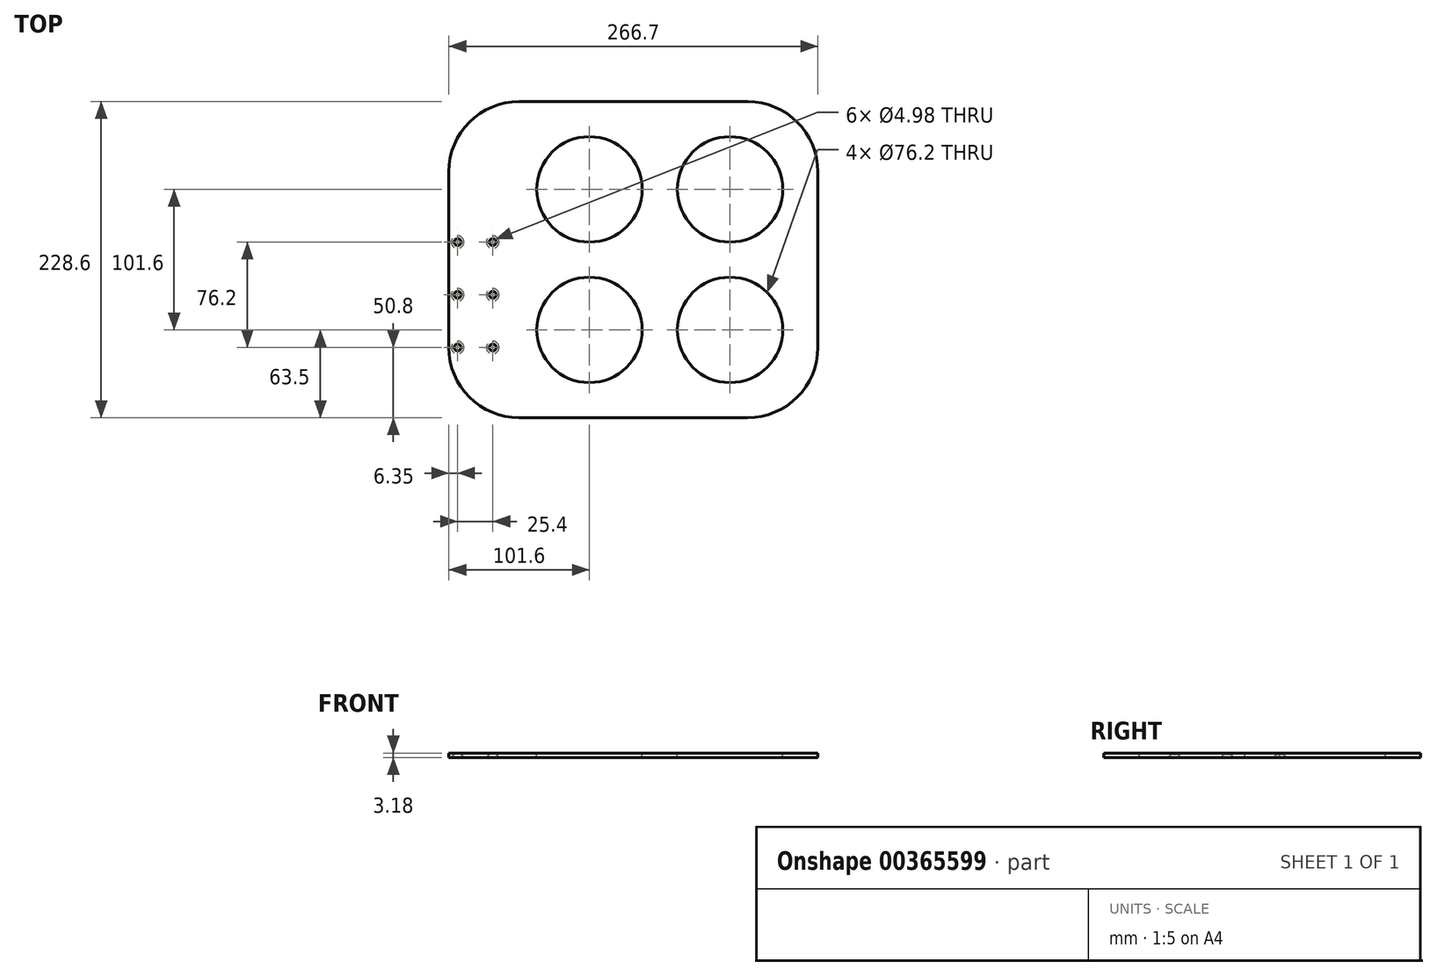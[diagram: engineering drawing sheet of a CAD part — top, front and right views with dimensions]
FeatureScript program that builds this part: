
annotation { "Feature Type Name" : "Feature", "Feature Type Description" : "" }
export const myFeature = defineFeature(function(context is Context, id is Id, definition is map)
    precondition{}
    {
        {
            var Q0;
            Q0=qCreatedBy(makeId("Top.planeOp"),FACE);
            var sketch = newSketch(context, id + "F0", { "sketchPlane" : qUnion([Q0])});
            skLineSegment(sketch, "E0.bottom", {"start": v(133.35, -114.3) * mm, "end": v(-133.35, -114.3) * mm});
            skLineSegment(sketch, "E0.top", {"start": v(133.35, 114.3) * mm, "end": v(-133.35, 114.3) * mm});
            skLineSegment(sketch, "E0.left", {"start": v(133.35, -114.3) * mm, "end": v(133.35, 114.3) * mm});
            skLineSegment(sketch, "E0.right", {"start": v(-133.35, -114.3) * mm, "end": v(-133.35, 114.3) * mm});
            skPoint(sketch, "E0.middle", {"position": v(0, 0) * mm});
            skSolve(sketch);
        }
        {
            var Q0;
            Q0=makeQuery(id+"F0.imprint","IMPRINT",FACE,{"disambiguationData":[TD([[makeQuery(id+"F0.imprint","IMPRINT",EDGE,{"derivedFrom":sQuery(id+"F0.wireOp",EDGE,"E0.bottom")}),-1.0]])]});
            extrude(context, id + "F1", {"entities" : qUnion([Q0]), "depth" : 3.17 * mm, "offsetDistance" : 25.4 * mm});
        }
        {
            var Q0;
            Q0=makeQuery(id+"F1.opExtrude","SWEPT_EDGE",EDGE,{"disambiguationData":[OSD([sQuery(id+"F0.wireOp",EDGE,"E0.top"),sQuery(id+"F0.wireOp",EDGE,"E0.right")])]});
            var Q1;
            Q1=makeQuery(id+"F1.opExtrude","SWEPT_EDGE",EDGE,{"disambiguationData":[OSD([sQuery(id+"F0.wireOp",EDGE,"E0.top"),sQuery(id+"F0.wireOp",EDGE,"E0.left")])]});
            var Q2;
            Q2=makeQuery(id+"F1.opExtrude","SWEPT_EDGE",EDGE,{"disambiguationData":[OSD([sQuery(id+"F0.wireOp",EDGE,"E0.bottom"),sQuery(id+"F0.wireOp",EDGE,"E0.left")])]});
            var Q3;
            Q3=makeQuery(id+"F1.opExtrude","SWEPT_EDGE",EDGE,{"disambiguationData":[OSD([sQuery(id+"F0.wireOp",EDGE,"E0.bottom"),sQuery(id+"F0.wireOp",EDGE,"E0.right")])]});
            fillet(context, id + "F2", {"entities" : qUnion([Q0, Q1, Q2, Q3]), "radius" : 50.8 * mm, "tangentPropagation" : true, "allowEdgeOverflow" : false});
        }
        {
            var Q0;
            Q0=makeQuery(id+"F1.opExtrude","CAP_FACE",FACE,{"disambiguationData":[OSD([sQuery(id+"F0.wireOp",EDGE,"E0.bottom"),sQuery(id+"F0.wireOp",EDGE,"E0.top"),sQuery(id+"F0.wireOp",EDGE,"E0.left"),sQuery(id+"F0.wireOp",EDGE,"E0.right")])],"isStart":true});
            var sketch = newSketch(context, id + "F3", { "sketchPlane" : qUnion([Q0])});
            skPoint(sketch, "E1", {"position": v(-127, 63.5) * mm});
            skPoint(sketch, "E2", {"position": v(-127, 25.4) * mm});
            skPoint(sketch, "E3", {"position": v(-127, -12.7) * mm});
            skPoint(sketch, "E4", {"position": v(-101.6, 63.5) * mm});
            skPoint(sketch, "E5", {"position": v(-101.6, 25.4) * mm});
            skPoint(sketch, "E6", {"position": v(-101.6, -12.7) * mm});
            skSolve(sketch);
        }
        {
            var Q0;
            Q0=sQuery(id+"F3.wireOp",VERTEX,"E3");
            var Q1;
            Q1=sQuery(id+"F3.wireOp",VERTEX,"E6");
            var Q2;
            Q2=sQuery(id+"F3.wireOp",VERTEX,"E5");
            var Q3;
            Q3=sQuery(id+"F3.wireOp",VERTEX,"E2");
            var Q4;
            Q4=sQuery(id+"F3.wireOp",VERTEX,"E1");
            var Q5;
            Q5=sQuery(id+"F3.wireOp",VERTEX,"E4");
            var Q6;
            Q6=makeQuery(id+"F1.opExtrude","SWEPT_BODY",BODY,{"disambiguationData":[OSD([sQuery(id+"F0.wireOp",EDGE,"E0.bottom"),sQuery(id+"F0.wireOp",EDGE,"E0.top"),sQuery(id+"F0.wireOp",EDGE,"E0.left"),sQuery(id+"F0.wireOp",EDGE,"E0.right")])]});
            hole(context, id + "F4", {"style" : HoleStyle.C_SINK, "endStyle" : HoleEndStyle.THROUGH, "standardTappedOrClearance" : lookupTablePath({ "fit" : "Normal (ASME)", "standard" : "ANSI", "size" : "#8", "type" : "Clearance" }), "standardBlindInLast" : lookupTablePath({ "fit" : "Normal", "standard" : "ANSI", "size" : "#8", "type" : "Clearance" }), "holeDiameter" : 4.98 * mm, "cSinkDiameter" : 9.12 * mm, "cSinkAngle" : 82 * degree, "majorDiameter" : 4.17 * mm, "isTappedThrough" : true, "tappedDepth" : 12.7 * mm, "tapClearance" : 3, "locations" : qUnion([Q0, Q1, Q2, Q3, Q4, Q5]), "scope" : qUnion([Q6]), "startStyle" : HoleStartStyle.SKETCH});
        }
        {
            var Q0;
            Q0=makeQuery(id+"F1.opExtrude","CAP_FACE",FACE,{"disambiguationData":[OSD([sQuery(id+"F0.wireOp",EDGE,"E0.bottom"),sQuery(id+"F0.wireOp",EDGE,"E0.top"),sQuery(id+"F0.wireOp",EDGE,"E0.left"),sQuery(id+"F0.wireOp",EDGE,"E0.right")])],"isStart":false});
            var sketch = newSketch(context, id + "F5", { "sketchPlane" : qUnion([Q0])});
            skPoint(sketch, "E7", {"position": v(-31.75, 50.8) * mm});
            skPoint(sketch, "E8", {"position": v(69.85, 50.8) * mm});
            skPoint(sketch, "E9", {"position": v(69.85, -50.8) * mm});
            skPoint(sketch, "E10", {"position": v(-31.75, -50.8) * mm});
            skCircle(sketch, "E11", {"center": v(-31.75, 50.8) * mm, "radius": 38.1 * mm});
            skCircle(sketch, "E12", {"center": v(69.85, 50.8) * mm, "radius": 38.1 * mm});
            skCircle(sketch, "E13", {"center": v(-31.75, -50.8) * mm, "radius": 38.1 * mm});
            skCircle(sketch, "E14", {"center": v(69.85, -50.8) * mm, "radius": 38.1 * mm});
            skSolve(sketch);
        }
        {
            var Q0;
            Q0 = qSketchRegion(id + "F5", true);
            extrude(context, id + "F6", {"entities" : qUnion([Q0]), "operationType" : NewBodyOperationType.REMOVE, "endBound" : BoundingType.THROUGH_ALL, "oppositeDirection" : true, "depth" : 25.4 * mm, "offsetDistance" : 25.4 * mm});
        }
    });
